# Revit family: Domotics-DomesticRanges-GEWISS-27COMBI_SYSTEM-IP55_1P_2P_3P_4P
name_source: partatom
category: Apparecchi elettrici
revit_build: Autodesk Revit 2016 (Build: 20161004_0715(x64)
units: mm (PartAtom-declared; Revit-internal decimal feet)

## family parameters
Condiviso = No
Host = Superficie
Mantenere orientamento annotazione = No
Numero OmniClass = 23.80.30.14.24
Punto di calcolo locali = No
Quota connettore circolare = Usa diametro
Taglio con vuoti quando caricato = Sì
Tipo di parte = Normale
Titolo OmniClass = Junction Boxes

## types (1)
- Domotics-DomesticRanges-GEWISS-27COMBI_SYSTEM-IP55_1P_2P_3P_4P
    Catalogue = DOMOTICS
    Catalogue Range = 27COMBI
    Colour = Grey RAL 7035
    Description: = 4 gang
    Descrizione = HORIZ.4(4x1) GANG ENCLOSURE IP55
    Door colour: = Transparent
    Door type = With membrane
    EAN code = 8011564055391
    Electrocod = 0212
    Glow Wire Test = 650°C
    IDF = ca9a8566-e3d3-440d-b06c-67991be3eed3
    IDT = 3807d107-ecc7-4bef-bd8b-fcc875e0ad94
    IP degree = IP55
    Immagine tipo = GW27044.jpg
    Installation temperature = -25 +60 °C
    Insulation class = II
    Larghezza = 132 mm  [stored 0.433071 ft]
    Lid screws = Stainless steel
    Modello = GW27044
    No. SYSTEM modules = 4 gang
    No. knockout holes Ã˜23 = 8 on sides / 1 on the bottom
    Outer dim. LxHxD (mm) = 132x82x65
    Produttore = GEWISS S.p.A.
    Prospetto di default = 1219 mm
    SEO = Enclosure
    Shock resistance = IK07
    Standard; = EN 60670-1
    Technical sheet = https://www.gewiss.com
    Thermo-pressure with ball = 70
    Tipo = SYSTEM COMBI CONTENITORI IP55_BASE : GW27044 - 4 POSTO
    Torque screws tightening = 0,8NM
    Type of knockout holes = Removable with tool
    URL = https://www.gewiss.com
    Version file RFA = 19.4

note: source unit labels omitted for Thermo-pressure with ball — the stored unit's dimension contradicts the parameter name (converter mislabeling)

note: [stored X ft] marks values corroborated as IEEE doubles in the binary element streams (Revit-internal decimal feet)
